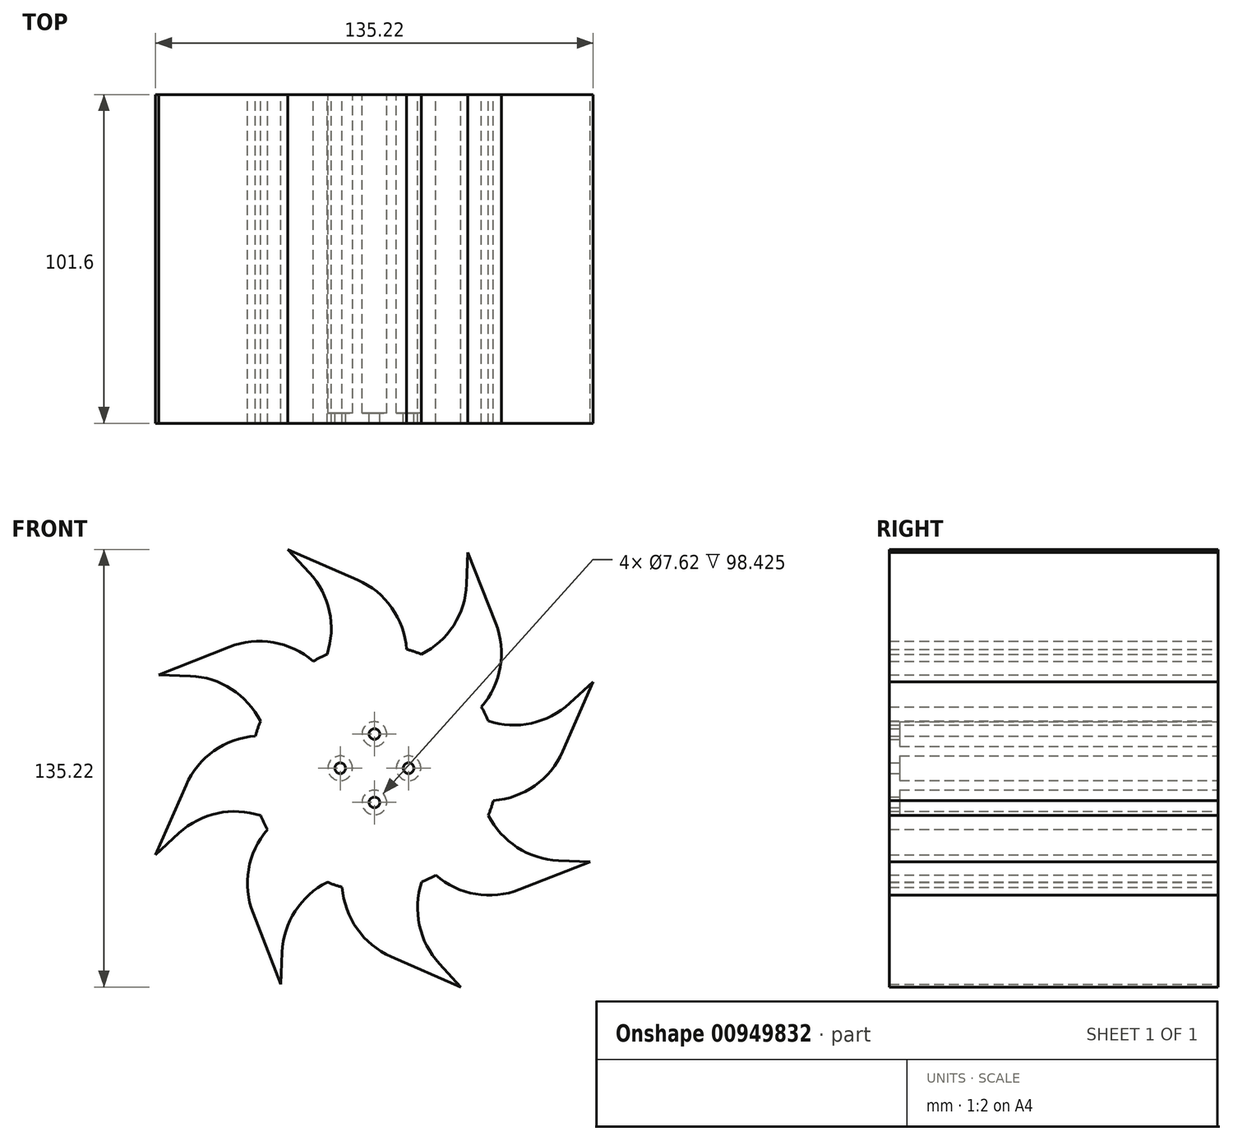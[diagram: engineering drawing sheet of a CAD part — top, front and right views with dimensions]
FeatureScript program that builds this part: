
annotation { "Feature Type Name" : "Feature", "Feature Type Description" : "" }
export const myFeature = defineFeature(function(context is Context, id is Id, definition is map)
    precondition{}
    {
        {
            var Q0;
            Q0=qCreatedBy(makeId("Front.planeOp"),FACE);
            var sketch = newSketch(context, id + "F0", { "sketchPlane" : qUnion([Q0])});
            skCircle(sketch, "E0.2.0", {"center": v(0, 0) * mm, "radius": 38.1 * mm});
            skPoint(sketch, "E0.center", {"position": v(0, 0) * mm});
            skLineSegment(sketch, "E1", {"start": v(-14.63, 35.18) * mm, "end": v(-9.77, 49.21) * mm});
            skLineSegment(sketch, "E2", {"start": v(-9.77, 49.21) * mm, "end": v(-26.73, 67.61) * mm});
            skLineSegment(sketch, "E3", {"start": v(-26.73, 67.61) * mm, "end": v(15.4, 49.21) * mm});
            skLineSegment(sketch, "E4", {"start": v(15.4, 49.21) * mm, "end": v(9.97, 36.77) * mm});
            skLineSegment(sketch, "E5.1.0", {"start": v(-66.71, 28.9) * mm, "end": v(-23.9, 45.69) * mm});
            skLineSegment(sketch, "E5.1.1", {"start": v(-41.7, 27.9) * mm, "end": v(-66.71, 28.9) * mm});
            skLineSegment(sketch, "E5.1.2", {"start": v(-35.22, 14.53) * mm, "end": v(-41.7, 27.9) * mm});
            skLineSegment(sketch, "E5.1.3", {"start": v(-23.9, 45.69) * mm, "end": v(-18.95, 33.05) * mm});
            skLineSegment(sketch, "E5.2.0", {"start": v(-67.61, -26.73) * mm, "end": v(-49.21, 15.4) * mm});
            skLineSegment(sketch, "E5.2.1", {"start": v(-49.21, -9.77) * mm, "end": v(-67.61, -26.73) * mm});
            skLineSegment(sketch, "E5.2.2", {"start": v(-35.18, -14.63) * mm, "end": v(-49.21, -9.77) * mm});
            skLineSegment(sketch, "E5.2.3", {"start": v(-49.21, 15.4) * mm, "end": v(-36.77, 9.97) * mm});
            skLineSegment(sketch, "E5.3.0", {"start": v(-28.9, -66.71) * mm, "end": v(-45.69, -23.9) * mm});
            skLineSegment(sketch, "E5.3.1", {"start": v(-27.9, -41.7) * mm, "end": v(-28.9, -66.71) * mm});
            skLineSegment(sketch, "E5.3.2", {"start": v(-14.53, -35.22) * mm, "end": v(-27.9, -41.7) * mm});
            skLineSegment(sketch, "E5.3.3", {"start": v(-45.69, -23.9) * mm, "end": v(-33.05, -18.95) * mm});
            skLineSegment(sketch, "E5.4.0", {"start": v(26.73, -67.61) * mm, "end": v(-15.4, -49.21) * mm});
            skLineSegment(sketch, "E5.4.1", {"start": v(9.77, -49.21) * mm, "end": v(26.73, -67.61) * mm});
            skLineSegment(sketch, "E5.4.2", {"start": v(14.63, -35.18) * mm, "end": v(9.77, -49.21) * mm});
            skLineSegment(sketch, "E5.4.3", {"start": v(-15.4, -49.21) * mm, "end": v(-9.97, -36.77) * mm});
            skLineSegment(sketch, "E5.5.0", {"start": v(66.71, -28.9) * mm, "end": v(23.9, -45.69) * mm});
            skLineSegment(sketch, "E5.5.1", {"start": v(41.7, -27.9) * mm, "end": v(66.71, -28.9) * mm});
            skLineSegment(sketch, "E5.5.2", {"start": v(35.22, -14.53) * mm, "end": v(41.7, -27.9) * mm});
            skLineSegment(sketch, "E5.5.3", {"start": v(23.9, -45.69) * mm, "end": v(18.95, -33.05) * mm});
            skLineSegment(sketch, "E5.6.0", {"start": v(67.61, 26.73) * mm, "end": v(49.21, -15.4) * mm});
            skLineSegment(sketch, "E5.6.1", {"start": v(49.21, 9.77) * mm, "end": v(67.61, 26.73) * mm});
            skLineSegment(sketch, "E5.6.2", {"start": v(35.18, 14.63) * mm, "end": v(49.21, 9.77) * mm});
            skLineSegment(sketch, "E5.6.3", {"start": v(49.21, -15.4) * mm, "end": v(36.77, -9.97) * mm});
            skLineSegment(sketch, "E5.7.0", {"start": v(28.9, 66.71) * mm, "end": v(45.69, 23.9) * mm});
            skLineSegment(sketch, "E5.7.1", {"start": v(27.9, 41.7) * mm, "end": v(28.9, 66.71) * mm});
            skLineSegment(sketch, "E5.7.2", {"start": v(14.53, 35.22) * mm, "end": v(27.9, 41.7) * mm});
            skLineSegment(sketch, "E5.7.3", {"start": v(45.69, 23.9) * mm, "end": v(33.05, 18.95) * mm});
            skSolve(sketch);
        }
        {
            var Q0;
            {var subQ0=sQuery(id+"F0.wireOp",EDGE,"E0.2.0");var subQ4=makeQuery(id+"F0.imprint","INTERSECT",VERTEX,{"derivedFrom":[subQ0,sQuery(id+"F0.wireOp",EDGE,"E5.3.2")]});Q0=makeQuery(id+"F0.imprint","IMPRINT",FACE,{"disambiguationData":[TD([[makeQuery(id+"F0.imprint","IMPRINT",EDGE,{"disambiguationData":[TD([[subQ4,-1.0]])],"derivedFrom":subQ0}),1.0]])]});}
            var Q1;
            {var subQ1=sQuery(id+"F0.wireOp",EDGE,"E5.1.0");Q1=makeQuery(id+"F0.imprint","IMPRINT",FACE,{"disambiguationData":[TD([[makeQuery(id+"F0.imprint","IMPRINT",EDGE,{"derivedFrom":subQ1}),-1.0]])]});}
            var Q2;
            {var subQ0=sQuery(id+"F0.wireOp",EDGE,"E1");Q2=makeQuery(id+"F0.imprint","IMPRINT",FACE,{"disambiguationData":[TD([[makeQuery(id+"F0.imprint","IMPRINT",EDGE,{"derivedFrom":subQ0}),-1.0]])]});}
            var Q3;
            Q3=makeQuery(id+"F0.imprint","IMPRINT",FACE,{"disambiguationData":[TD([[makeQuery(id+"F0.imprint","IMPRINT",EDGE,{"derivedFrom":sQuery(id+"F0.wireOp",EDGE,"E5.7.0")}),-1.0]])]});
            var Q4;
            Q4=makeQuery(id+"F0.imprint","IMPRINT",FACE,{"disambiguationData":[TD([[makeQuery(id+"F0.imprint","IMPRINT",EDGE,{"derivedFrom":sQuery(id+"F0.wireOp",EDGE,"E5.6.0")}),-1.0]])]});
            var Q5;
            Q5=makeQuery(id+"F0.imprint","IMPRINT",FACE,{"disambiguationData":[TD([[makeQuery(id+"F0.imprint","IMPRINT",EDGE,{"derivedFrom":sQuery(id+"F0.wireOp",EDGE,"E5.5.0")}),-1.0]])]});
            var Q6;
            {var subQ5=sQuery(id+"F0.wireOp",EDGE,"E5.4.0");Q6=makeQuery(id+"F0.imprint","IMPRINT",FACE,{"disambiguationData":[TD([[makeQuery(id+"F0.imprint","IMPRINT",EDGE,{"derivedFrom":subQ5}),-1.0]])]});}
            var Q7;
            {var subQ4=sQuery(id+"F0.wireOp",EDGE,"E5.3.0");Q7=makeQuery(id+"F0.imprint","IMPRINT",FACE,{"disambiguationData":[TD([[makeQuery(id+"F0.imprint","IMPRINT",EDGE,{"derivedFrom":subQ4}),-1.0]])]});}
            var Q8;
            {var subQ4=sQuery(id+"F0.wireOp",EDGE,"E5.2.0");Q8=makeQuery(id+"F0.imprint","IMPRINT",FACE,{"disambiguationData":[TD([[makeQuery(id+"F0.imprint","IMPRINT",EDGE,{"derivedFrom":subQ4}),-1.0]])]});}
            extrude(context, id + "F1", {"entities" : qUnion([Q0, Q1, Q2, Q3, Q4, Q5, Q6, Q7, Q8]), "depth" : 101.6 * mm, "offsetDistance" : 25.4 * mm});
        }
        {
            var Q0;
            Q0=makeQuery(id+"F1.opExtrude","SWEPT_EDGE",EDGE,{"disambiguationData":[OSD([sQuery(id+"F0.wireOp",EDGE,"E5.2.0"),sQuery(id+"F0.wireOp",EDGE,"E5.2.3")])]});
            var Q1;
            Q1=makeQuery(id+"F1.opExtrude","SWEPT_EDGE",EDGE,{"disambiguationData":[OSD([sQuery(id+"F0.wireOp",EDGE,"E5.1.0"),sQuery(id+"F0.wireOp",EDGE,"E5.1.3")])]});
            var Q2;
            Q2=makeQuery(id+"F1.opExtrude","SWEPT_EDGE",EDGE,{"disambiguationData":[OSD([sQuery(id+"F0.wireOp",EDGE,"E5.1.1"),sQuery(id+"F0.wireOp",EDGE,"E5.1.2")])]});
            var Q3;
            Q3=makeQuery(id+"F1.opExtrude","SWEPT_EDGE",EDGE,{"disambiguationData":[OSD([sQuery(id+"F0.wireOp",EDGE,"E3"),sQuery(id+"F0.wireOp",EDGE,"E4")])]});
            var Q4;
            Q4=makeQuery(id+"F1.opExtrude","SWEPT_EDGE",EDGE,{"disambiguationData":[OSD([sQuery(id+"F0.wireOp",EDGE,"E5.7.0"),sQuery(id+"F0.wireOp",EDGE,"E5.7.3")])]});
            var Q5;
            Q5=makeQuery(id+"F1.opExtrude","SWEPT_EDGE",EDGE,{"disambiguationData":[OSD([sQuery(id+"F0.wireOp",EDGE,"E5.6.0"),sQuery(id+"F0.wireOp",EDGE,"E5.6.3")])]});
            var Q6;
            Q6=makeQuery(id+"F1.opExtrude","SWEPT_EDGE",EDGE,{"disambiguationData":[OSD([sQuery(id+"F0.wireOp",EDGE,"E5.5.0"),sQuery(id+"F0.wireOp",EDGE,"E5.5.3")])]});
            var Q7;
            Q7=makeQuery(id+"F1.opExtrude","SWEPT_EDGE",EDGE,{"disambiguationData":[OSD([sQuery(id+"F0.wireOp",EDGE,"E5.4.0"),sQuery(id+"F0.wireOp",EDGE,"E5.4.3")])]});
            var Q8;
            Q8=makeQuery(id+"F1.opExtrude","SWEPT_EDGE",EDGE,{"disambiguationData":[OSD([sQuery(id+"F0.wireOp",EDGE,"E5.3.0"),sQuery(id+"F0.wireOp",EDGE,"E5.3.3")])]});
            var Q9;
            Q9=makeQuery(id+"F1.opExtrude","SWEPT_EDGE",EDGE,{"disambiguationData":[OSD([sQuery(id+"F0.wireOp",EDGE,"E5.2.1"),sQuery(id+"F0.wireOp",EDGE,"E5.2.2")])]});
            var Q10;
            Q10=makeQuery(id+"F1.opExtrude","SWEPT_EDGE",EDGE,{"disambiguationData":[OSD([sQuery(id+"F0.wireOp",EDGE,"E5.3.1"),sQuery(id+"F0.wireOp",EDGE,"E5.3.2")])]});
            var Q11;
            Q11=makeQuery(id+"F1.opExtrude","SWEPT_EDGE",EDGE,{"disambiguationData":[OSD([sQuery(id+"F0.wireOp",EDGE,"E5.4.1"),sQuery(id+"F0.wireOp",EDGE,"E5.4.2")])]});
            var Q12;
            Q12=makeQuery(id+"F1.opExtrude","SWEPT_EDGE",EDGE,{"disambiguationData":[OSD([sQuery(id+"F0.wireOp",EDGE,"E5.5.1"),sQuery(id+"F0.wireOp",EDGE,"E5.5.2")])]});
            var Q13;
            Q13=makeQuery(id+"F1.opExtrude","SWEPT_EDGE",EDGE,{"disambiguationData":[OSD([sQuery(id+"F0.wireOp",EDGE,"E5.6.1"),sQuery(id+"F0.wireOp",EDGE,"E5.6.2")])]});
            var Q14;
            Q14=makeQuery(id+"F1.opExtrude","SWEPT_EDGE",EDGE,{"disambiguationData":[OSD([sQuery(id+"F0.wireOp",EDGE,"E5.7.1"),sQuery(id+"F0.wireOp",EDGE,"E5.7.2")])]});
            var Q15;
            Q15=makeQuery(id+"F1.opExtrude","SWEPT_EDGE",EDGE,{"disambiguationData":[OSD([sQuery(id+"F0.wireOp",EDGE,"E1"),sQuery(id+"F0.wireOp",EDGE,"E2")])]});
            fillet(context, id + "F2", {"entities" : qUnion([Q0, Q1, Q2, Q3, Q4, Q5, Q6, Q7, Q8, Q9, Q10, Q11, Q12, Q13, Q14, Q15]), "radius" : 25.4 * mm, "tangentPropagation" : true, "allowEdgeOverflow" : false});
        }
        {
            var Q0;
            Q0=makeQuery(id+"F1.opExtrude","CAP_FACE",FACE,{"disambiguationData":[OSD([sQuery(id+"F0.wireOp",EDGE,"E0.2.0"),sQuery(id+"F0.wireOp",EDGE,"E1"),sQuery(id+"F0.wireOp",EDGE,"E2"),sQuery(id+"F0.wireOp",EDGE,"E3"),sQuery(id+"F0.wireOp",EDGE,"E4"),sQuery(id+"F0.wireOp",EDGE,"E5.1.0"),sQuery(id+"F0.wireOp",EDGE,"E5.1.1"),sQuery(id+"F0.wireOp",EDGE,"E5.1.2"),sQuery(id+"F0.wireOp",EDGE,"E5.1.3"),sQuery(id+"F0.wireOp",EDGE,"E5.2.0"),sQuery(id+"F0.wireOp",EDGE,"E5.2.1"),sQuery(id+"F0.wireOp",EDGE,"E5.2.2"),sQuery(id+"F0.wireOp",EDGE,"E5.2.3"),sQuery(id+"F0.wireOp",EDGE,"E5.3.0"),sQuery(id+"F0.wireOp",EDGE,"E5.3.1"),sQuery(id+"F0.wireOp",EDGE,"E5.3.2"),sQuery(id+"F0.wireOp",EDGE,"E5.3.3"),sQuery(id+"F0.wireOp",EDGE,"E5.4.0"),sQuery(id+"F0.wireOp",EDGE,"E5.4.1"),sQuery(id+"F0.wireOp",EDGE,"E5.4.2"),sQuery(id+"F0.wireOp",EDGE,"E5.4.3"),sQuery(id+"F0.wireOp",EDGE,"E5.5.0"),sQuery(id+"F0.wireOp",EDGE,"E5.5.1"),sQuery(id+"F0.wireOp",EDGE,"E5.5.2"),sQuery(id+"F0.wireOp",EDGE,"E5.5.3"),sQuery(id+"F0.wireOp",EDGE,"E5.6.0"),sQuery(id+"F0.wireOp",EDGE,"E5.6.1"),sQuery(id+"F0.wireOp",EDGE,"E5.6.2"),sQuery(id+"F0.wireOp",EDGE,"E5.6.3"),sQuery(id+"F0.wireOp",EDGE,"E5.7.0"),sQuery(id+"F0.wireOp",EDGE,"E5.7.1"),sQuery(id+"F0.wireOp",EDGE,"E5.7.2"),sQuery(id+"F0.wireOp",EDGE,"E5.7.3")])],"isStart":true});
            var sketch = newSketch(context, id + "F3", { "sketchPlane" : qUnion([Q0])});
            skCircle(sketch, "E6", {"center": v(0, 0) * mm, "radius": 17.11 * mm});
            skCircle(sketch, "E7", {"center": v(0, 10.57) * mm, "radius": 1.65 * mm});
            skCircle(sketch, "E8.1.0", {"center": v(-10.57, 0) * mm, "radius": 1.65 * mm});
            skCircle(sketch, "E8.2.0", {"center": v(0, -10.57) * mm, "radius": 1.65 * mm});
            skCircle(sketch, "E8.3.0", {"center": v(10.57, 0) * mm, "radius": 1.65 * mm});
            skSolve(sketch);
        }
        {
            var Q0;
            Q0=makeQuery(id+"F3.imprint","IMPRINT",FACE,{"disambiguationData":[TD([[makeQuery(id+"F3.imprint","IMPRINT",EDGE,{"derivedFrom":sQuery(id+"F3.wireOp",EDGE,"E7")}),1.0]])]});
            var Q1;
            Q1=makeQuery(id+"F3.imprint","IMPRINT",FACE,{"disambiguationData":[TD([[makeQuery(id+"F3.imprint","IMPRINT",EDGE,{"derivedFrom":sQuery(id+"F3.wireOp",EDGE,"E8.1.0")}),1.0]])]});
            var Q2;
            Q2=makeQuery(id+"F3.imprint","IMPRINT",FACE,{"disambiguationData":[TD([[makeQuery(id+"F3.imprint","IMPRINT",EDGE,{"derivedFrom":sQuery(id+"F3.wireOp",EDGE,"E8.3.0")}),1.0]])]});
            var Q3;
            Q3=makeQuery(id+"F3.imprint","IMPRINT",FACE,{"disambiguationData":[TD([[makeQuery(id+"F3.imprint","IMPRINT",EDGE,{"derivedFrom":sQuery(id+"F3.wireOp",EDGE,"E8.2.0")}),1.0]])]});
            extrude(context, id + "F4", {"entities" : qUnion([Q0, Q1, Q2, Q3]), "operationType" : NewBodyOperationType.REMOVE, "oppositeDirection" : true, "depth" : 127 * mm, "offsetDistance" : 25.4 * mm});
        }
        {
            var Q0;
            Q0=makeQuery(id+"F1.opExtrude","CAP_FACE",FACE,{"disambiguationData":[OSD([sQuery(id+"F0.wireOp",EDGE,"E0.2.0"),sQuery(id+"F0.wireOp",EDGE,"E1"),sQuery(id+"F0.wireOp",EDGE,"E2"),sQuery(id+"F0.wireOp",EDGE,"E3"),sQuery(id+"F0.wireOp",EDGE,"E4"),sQuery(id+"F0.wireOp",EDGE,"E5.1.0"),sQuery(id+"F0.wireOp",EDGE,"E5.1.1"),sQuery(id+"F0.wireOp",EDGE,"E5.1.2"),sQuery(id+"F0.wireOp",EDGE,"E5.1.3"),sQuery(id+"F0.wireOp",EDGE,"E5.2.0"),sQuery(id+"F0.wireOp",EDGE,"E5.2.1"),sQuery(id+"F0.wireOp",EDGE,"E5.2.2"),sQuery(id+"F0.wireOp",EDGE,"E5.2.3"),sQuery(id+"F0.wireOp",EDGE,"E5.3.0"),sQuery(id+"F0.wireOp",EDGE,"E5.3.1"),sQuery(id+"F0.wireOp",EDGE,"E5.3.2"),sQuery(id+"F0.wireOp",EDGE,"E5.3.3"),sQuery(id+"F0.wireOp",EDGE,"E5.4.0"),sQuery(id+"F0.wireOp",EDGE,"E5.4.1"),sQuery(id+"F0.wireOp",EDGE,"E5.4.2"),sQuery(id+"F0.wireOp",EDGE,"E5.4.3"),sQuery(id+"F0.wireOp",EDGE,"E5.5.0"),sQuery(id+"F0.wireOp",EDGE,"E5.5.1"),sQuery(id+"F0.wireOp",EDGE,"E5.5.2"),sQuery(id+"F0.wireOp",EDGE,"E5.5.3"),sQuery(id+"F0.wireOp",EDGE,"E5.6.0"),sQuery(id+"F0.wireOp",EDGE,"E5.6.1"),sQuery(id+"F0.wireOp",EDGE,"E5.6.2"),sQuery(id+"F0.wireOp",EDGE,"E5.6.3"),sQuery(id+"F0.wireOp",EDGE,"E5.7.0"),sQuery(id+"F0.wireOp",EDGE,"E5.7.1"),sQuery(id+"F0.wireOp",EDGE,"E5.7.2"),sQuery(id+"F0.wireOp",EDGE,"E5.7.3")])],"isStart":true});
            var sketch = newSketch(context, id + "F5", { "sketchPlane" : qUnion([Q0])});
            skCircle(sketch, "E9", {"center": v(0, 10.57) * mm, "radius": 3.81 * mm});
            skCircle(sketch, "E10.1.0", {"center": v(-10.57, 0) * mm, "radius": 3.81 * mm});
            skCircle(sketch, "E10.2.0", {"center": v(0, -10.57) * mm, "radius": 3.81 * mm});
            skCircle(sketch, "E10.3.0", {"center": v(10.57, 0) * mm, "radius": 3.81 * mm});
            skPoint(sketch, "E10.center", {"position": v(0, 0) * mm});
            skSolve(sketch);
        }
        {
            var Q0;
            Q0=makeQuery(id+"F5.imprint","IMPRINT",FACE,{"disambiguationData":[TD([[makeQuery(id+"F5.imprint","IMPRINT",EDGE,{"derivedFrom":sQuery(id+"F5.wireOp",EDGE,"E9")}),1.0]])]});
            var Q1;
            Q1=makeQuery(id+"F5.imprint","IMPRINT",FACE,{"disambiguationData":[TD([[makeQuery(id+"F5.imprint","IMPRINT",EDGE,{"derivedFrom":sQuery(id+"F5.wireOp",EDGE,"E10.3.0")}),1.0]])]});
            var Q2;
            Q2=makeQuery(id+"F5.imprint","IMPRINT",FACE,{"disambiguationData":[TD([[makeQuery(id+"F5.imprint","IMPRINT",EDGE,{"derivedFrom":sQuery(id+"F5.wireOp",EDGE,"E10.2.0")}),1.0]])]});
            var Q3;
            Q3=makeQuery(id+"F5.imprint","IMPRINT",FACE,{"disambiguationData":[TD([[makeQuery(id+"F5.imprint","IMPRINT",EDGE,{"derivedFrom":sQuery(id+"F5.wireOp",EDGE,"E10.1.0")}),1.0]])]});
            extrude(context, id + "F6", {"entities" : qUnion([Q0, Q1, Q2, Q3]), "operationType" : NewBodyOperationType.REMOVE, "oppositeDirection" : true, "depth" : 98.42 * mm, "offsetDistance" : 25.4 * mm});
        }
    });
